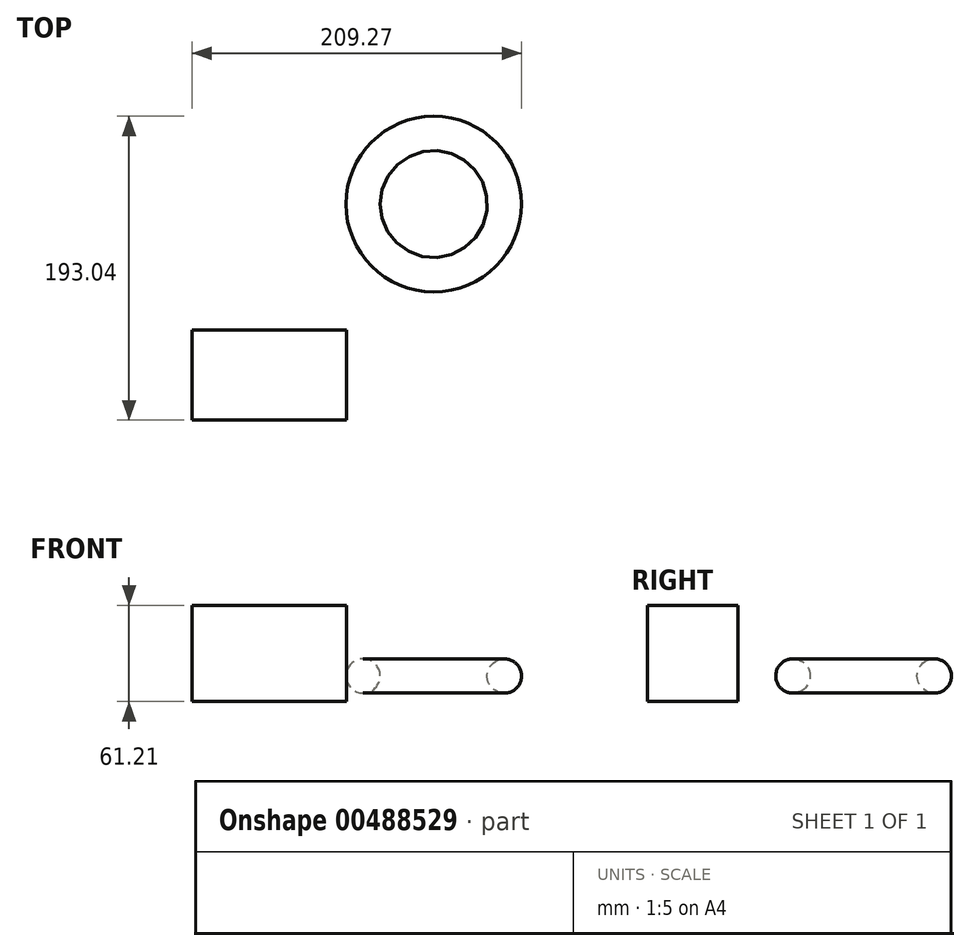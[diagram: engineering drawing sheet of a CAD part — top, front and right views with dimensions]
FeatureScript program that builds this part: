
annotation { "Feature Type Name" : "Feature", "Feature Type Description" : "" }
export const myFeature = defineFeature(function(context is Context, id is Id, definition is map)
    precondition{}
    {
        {
            var Q0;
            Q0=qCreatedBy(makeId("Front.planeOp"),FACE);
            var sketch = newSketch(context, id + "F0", { "sketchPlane" : qUnion([Q0])});
            skCircle(sketch, "E0", {"center": v(-44.88, 16.26) * mm, "radius": 10.9 * mm});
            skLineSegment(sketch, "E1", {"start": v(0, 0) * mm, "end": v(0, 53.46) * mm, "construction": true});
            skSolve(sketch);
        }
        {
            var Q0;
            Q0=makeQuery(id+"F0.imprint","IMPRINT",FACE,{"disambiguationData":[TD([[makeQuery(id+"F0.imprint","IMPRINT",EDGE,{"derivedFrom":sQuery(id+"F0.wireOp",EDGE,"E0")}),1.0]])]});
            var Q1;
            Q1=sQuery(id+"F0.wireOp",EDGE,"E0");
            var Q2;
            Q2=sQuery(id+"F0.wireOp",EDGE,"E1");
            revolve(context, id + "F1", {"entities" : qUnion([Q0]), "surfaceEntities" : qUnion([Q1]), "axis" : qUnion([Q2]), "revolveType" : RevolveType.FULL});
        }
        {
            var Q0;
            Q0=qCreatedBy(makeId("Top.planeOp"),FACE);
            var sketch = newSketch(context, id + "F2", { "sketchPlane" : qUnion([Q0])});
            skLineSegment(sketch, "E2.bottom", {"start": v(-55.4, -137.27) * mm, "end": v(-153.5, -137.27) * mm});
            skLineSegment(sketch, "E2.top", {"start": v(-55.4, -79.93) * mm, "end": v(-153.5, -79.93) * mm});
            skLineSegment(sketch, "E2.left", {"start": v(-55.4, -137.27) * mm, "end": v(-55.4, -79.93) * mm});
            skLineSegment(sketch, "E2.right", {"start": v(-153.5, -137.27) * mm, "end": v(-153.5, -79.93) * mm});
            skSolve(sketch);
        }
        {
            var Q0;
            Q0 = qSketchRegion(id + "F2", true);
            extrude(context, id + "F3", {"entities" : qUnion([Q0]), "depth" : 61.2 * mm});
        }
    });
